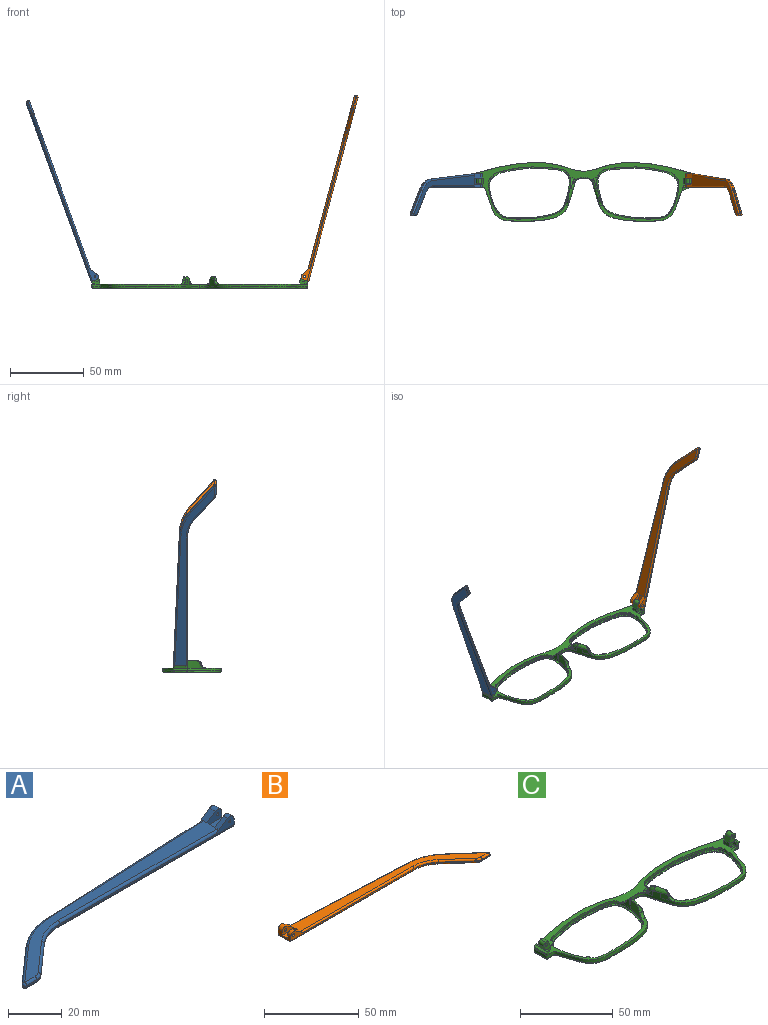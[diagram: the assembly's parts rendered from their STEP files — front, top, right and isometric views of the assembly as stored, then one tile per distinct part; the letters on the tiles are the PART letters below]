
ASSEMBLY  parts=3 mates=2
PART A: 43 faces, bbox 130.2x29.5x5.9 mm
  f0: plane 9.62x3.72mm, normal (1,0,0), area 24.7mm2, adj f1,f3,f4,f5,f10,f16,f18,f28
  f1: cylinder r=2.2mm len=3.45mm, axis (0,-1,0), area 11mm2, adj f0,f2,f4,f37
  f2: plane 6.01x3.91mm, normal (-0.55,0,0.84), area 12.7mm2, adj f1,f4,f9,f19,f37
  f3: plane 2.26x0.1mm, normal (0,0,1), area 0.1mm2, adj f0,f5,f18
  f4: plane 92.1x4.9mm, normal (0,-1,0), area 79.9mm2, adj f0,f1,f2,f14,f19,f36,f42
  f5: plane 93.42x4.13mm, normal (-0.04,1,0), area 64.8mm2, adj f0,f3,f11,f15,f17,f27,f28
  f6: plane 17.82x15.72mm, normal (-0.66,0.75,0), area 14.3mm2, adj f11,f12,f25,f30
  f7: plane 5.46x0.6mm, normal (0,-1,0), area 3.3mm2, adj f12,f13,f23,f32
  f8: plane 14.99x13.23mm, normal (0.66,-0.75,0), area 12mm2, adj f13,f14,f21,f34
  f9: plane 121.18x26.73mm, normal (0,0,1), area 627.7mm2, adj f2,f17,f19,f20,f21,f22,f23,f25
  f10: plane 129.1x27.08mm, normal (0,0,-1), area 686.5mm2, adj f0,f28,f29,f30,f32,f33,f34,f35
  f11: cylinder r=30mm len=18.52mm, axis (0,0,-1), area 12.2mm2, adj f5,f6,f26,f29
  f12: cylinder r=1mm len=1.75mm, axis (0,0,-1), area 1.5mm2, adj f6,f7,f24,f31
  f13: cylinder r=5mm len=3.31mm, axis (0,0,-1), area 2.2mm2, adj f7,f8,f22,f33
  f14: cylinder r=20mm len=13.23mm, axis (0,0,1), area 8.7mm2, adj f4,f8,f20,f35
  f15: plane 5.66x0.25mm, normal (0,0,-1), area 0.7mm2, adj f5,f17,f18
  f16: cylinder r=2.2mm len=3.45mm, axis (0,-1,0), area 14.8mm2, adj f0,f17,f18,f38
  f17: plane 6.01x3.91mm, normal (-0.55,0,0.84), area 16.9mm2, adj f5,f9,f15,f16,f18,f27,f38
  f18: plane 7.92x3.3mm, normal (0,1,0), area 15.9mm2, adj f0,f3,f15,f16,f17,f41
  f19: cylinder r=1mm len=84.18mm, axis (-1,0,0), area 131.4mm2, adj f2,f4,f9,f20
  f20: torus R=21mm, axis (0,0,1), area 23.1mm2, adj f9,f14,f19,f21
  f21: cylinder r=1mm len=15.65mm, axis (-0.75,-0.66,0), area 31.4mm2, adj f8,f9,f20,f22
  f22: torus R=4mm, axis (0,0,1), area 5.3mm2, adj f9,f13,f21,f23
  f23: cylinder r=1mm len=5.46mm, axis (-1,0,0), area 8.6mm2, adj f7,f9,f22,f24
  f24: sphere r=1mm, area 2.4mm2, adj f12,f23,f25
  f25: cylinder r=1mm len=18.48mm, axis (0.75,0.66,0), area 37.3mm2, adj f6,f9,f24,f26
  f26: torus R=29mm, axis (0,0,1), area 31.6mm2, adj f9,f11,f25,f27
  f27: cylinder r=1mm len=85.5mm, axis (1,0.04,0), area 133.5mm2, adj f5,f9,f17,f26
  f28: cylinder r=1mm len=93.46mm, axis (-1,-0.04,0), area 146.9mm2, adj f0,f5,f10,f29
  f29: torus R=29mm, axis (0,0,1), area 31.6mm2, adj f10,f11,f28,f30
  f30: cylinder r=1mm len=18.48mm, axis (-0.75,-0.66,0), area 37.3mm2, adj f6,f10,f29,f31
  f31: sphere r=1mm, area 2.4mm2, adj f12,f30,f32
  f32: cylinder r=1mm len=5.46mm, axis (1,0,0), area 8.6mm2, adj f7,f10,f31,f33
  f33: torus R=4mm, axis (0,0,1), area 5.3mm2, adj f10,f13,f32,f34
  f34: cylinder r=1mm len=15.65mm, axis (0.75,0.66,0), area 31.4mm2, adj f8,f10,f33,f35
  f35: torus R=21mm, axis (0,0,1), area 23.1mm2, adj f10,f14,f34,f36
  f36: cylinder r=1mm len=92.1mm, axis (1,0,0), area 144.7mm2, adj f0,f4,f10,f35
  f37: plane 7.92x4.7mm, normal (0,1,0), area 27mm2, adj f0,f1,f2,f39,f40,f42
  f38: plane 7.92x4.7mm, normal (0,-1,0), area 27mm2, adj f0,f16,f17,f39,f40,f41
  f39: plane 7.92x4.1mm, normal (0,0,1), area 32.5mm2, adj f0,f37,f38,f40
  f40: plane 4.1x1.4mm, normal (1,0,0), area 5.7mm2, adj f9,f37,f38,f39
  f41: cylinder r=0.5mm len=3.1mm, axis (0,-1,0), area 9.7mm2, adj f18,f38
  f42: cylinder r=0.5mm len=2.3mm, axis (0,-1,0), area 7.2mm2, adj f4,f37
PART B: 43 faces, bbox 130.2x29.5x5.9 mm
  f0: plane 9.62x3.72mm, normal (-1,0,0), area 24.7mm2, adj f1,f3,f4,f5,f10,f16,f18,f28
  f1: cylinder r=2.2mm len=3.45mm, axis (0,-1,0), area 11mm2, adj f0,f2,f4,f37
  f2: plane 6.01x3.91mm, normal (0.55,0,0.84), area 12.7mm2, adj f1,f4,f9,f19,f37
  f3: plane 2.26x0.1mm, normal (0,0,1), area 0.1mm2, adj f0,f5,f18
  f4: plane 92.1x4.9mm, normal (0,-1,0), area 78.2mm2, adj f0,f1,f2,f14,f19,f36,f42
  f5: plane 93.42x4.13mm, normal (0.04,1,0), area 64.8mm2, adj f0,f3,f11,f15,f17,f27,f28
  f6: plane 17.82x15.72mm, normal (0.66,0.75,0), area 14.3mm2, adj f11,f12,f25,f30
  f7: plane 5.46x0.6mm, normal (0,-1,0), area 3.3mm2, adj f12,f13,f23,f32
  f8: plane 14.99x13.23mm, normal (-0.66,-0.75,0), area 12mm2, adj f13,f14,f21,f34
  f9: plane 121.18x26.73mm, normal (0,0,1), area 627.7mm2, adj f2,f17,f19,f20,f21,f22,f23,f25
  f10: plane 129.1x27.08mm, normal (0,0,-1), area 686.5mm2, adj f0,f28,f29,f30,f32,f33,f34,f35
  f11: cylinder r=30mm len=18.52mm, axis (0,0,-1), area 12.2mm2, adj f5,f6,f26,f29
  f12: cylinder r=1mm len=1.75mm, axis (0,0,-1), area 1.5mm2, adj f6,f7,f24,f31
  f13: cylinder r=5mm len=3.31mm, axis (0,0,-1), area 2.2mm2, adj f7,f8,f22,f33
  f14: cylinder r=20mm len=13.23mm, axis (0,0,1), area 8.7mm2, adj f4,f8,f20,f35
  f15: plane 5.66x0.25mm, normal (0,0,-1), area 0.7mm2, adj f5,f17,f18
  f16: cylinder r=2.2mm len=3.45mm, axis (0,-1,0), area 14.8mm2, adj f0,f17,f18,f38
  f17: plane 6.01x3.91mm, normal (0.55,0,0.84), area 16.9mm2, adj f5,f9,f15,f16,f18,f27,f38
  f18: plane 7.92x3.3mm, normal (0,1,0), area 14.3mm2, adj f0,f3,f15,f16,f17,f41
  f19: cylinder r=1mm len=84.18mm, axis (1,0,0), area 131.4mm2, adj f2,f4,f9,f20
  f20: torus R=21mm, axis (0,0,1), area 23.1mm2, adj f9,f14,f19,f21
  f21: cylinder r=1mm len=15.65mm, axis (0.75,-0.66,0), area 31.4mm2, adj f8,f9,f20,f22
  f22: torus R=4mm, axis (0,0,1), area 5.3mm2, adj f9,f13,f21,f23
  f23: cylinder r=1mm len=5.46mm, axis (1,0,0), area 8.6mm2, adj f7,f9,f22,f24
  f24: sphere r=1mm, area 2.4mm2, adj f12,f23,f25
  f25: cylinder r=1mm len=18.48mm, axis (-0.75,0.66,0), area 37.3mm2, adj f6,f9,f24,f26
  f26: torus R=29mm, axis (0,0,1), area 31.6mm2, adj f9,f11,f25,f27
  f27: cylinder r=1mm len=85.5mm, axis (-1,0.04,0), area 133.5mm2, adj f5,f9,f17,f26
  f28: cylinder r=1mm len=93.46mm, axis (1,-0.04,0), area 146.9mm2, adj f0,f5,f10,f29
  f29: torus R=29mm, axis (0,0,1), area 31.6mm2, adj f10,f11,f28,f30
  f30: cylinder r=1mm len=18.48mm, axis (0.75,-0.66,0), area 37.3mm2, adj f6,f10,f29,f31
  f31: sphere r=1mm, area 2.4mm2, adj f12,f30,f32
  f32: cylinder r=1mm len=5.46mm, axis (-1,0,0), area 8.6mm2, adj f7,f10,f31,f33
  f33: torus R=4mm, axis (0,0,1), area 5.3mm2, adj f10,f13,f32,f34
  f34: cylinder r=1mm len=15.65mm, axis (-0.75,0.66,0), area 31.4mm2, adj f8,f10,f33,f35
  f35: torus R=21mm, axis (0,0,1), area 23.1mm2, adj f10,f14,f34,f36
  f36: cylinder r=1mm len=92.1mm, axis (-1,0,0), area 144.7mm2, adj f0,f4,f10,f35
  f37: plane 7.92x4.7mm, normal (0,1,0), area 25.4mm2, adj f0,f1,f2,f39,f40,f42
  f38: plane 7.92x4.7mm, normal (0,-1,0), area 25.4mm2, adj f0,f16,f17,f39,f40,f41
  f39: plane 7.92x4.1mm, normal (0,0,1), area 32.5mm2, adj f0,f37,f38,f40
  f40: plane 4.1x1.4mm, normal (-1,0,0), area 5.7mm2, adj f9,f37,f38,f39
  f41: cylinder r=0.88mm len=3.1mm, axis (0,-1,0), area 17mm2, adj f18,f38
  f42: cylinder r=0.88mm len=2.3mm, axis (0,-1,0), area 12.6mm2, adj f4,f37
PART C: 118 faces, bbox 148.1x40.9x17.9 mm
  f0: bspline ~1.82x1.22mm, area 0.7mm2, adj f2,f7,f37,f52
  f1: plane 147.69x40.46mm, normal (0,0,1), area 858.2mm2, adj f4,f5,f6,f7,f8,f12,f20,f23
  f2: bspline ~6.1x4.93mm, area 12.7mm2, adj f0,f7,f37,f41,f43,f52,f53
  f3: plane 4.46x1.45mm, normal (0,0,1), area 0.1mm2, adj f7,f38
  f4: plane 1.23x0.04mm, normal (0,0,1), area 0mm2, adj f1,f7,f22
  f5: plane 6.97x5.07mm, normal (0,1,0), area 22.7mm2, adj f1,f20,f21,f25,f27,f28,f30,f31
  f6: plane 3.2x2.36mm, normal (0,-1,0), area 5.7mm2, adj f1,f20,f26,f29
  f7: extruded ~73.26x39.84mm, area 292.7mm2, adj f0,f1,f2,f3,f4,f8,f13,f14
  f8: extruded ~35.39x5.69mm, area 72.2mm2, adj f1,f7,f18,f67
  f9: plane 144.78x37.85mm, normal (0,0,-1), area 582.4mm2, adj f13,f15,f17,f18,f19,f71,f73,f75
  f10: plane 56.06x35.45mm, normal (0,0,1), area 127mm2, adj f11,f19
  f11: extruded ~55.69x35.36mm, area 160.5mm2, adj f10,f12
  f12: extruded ~55.69x35.36mm, area 226.3mm2, adj f1,f11,f39,f40,f41,f42,f43,f44
  f13: bspline ~73.27x30.39mm, area 161.7mm2, adj f7,f9,f14,f71
  f14: bspline ~1x1mm, area 0.8mm2, adj f7,f13,f15
  f15: bspline ~8.99x1.23mm, area 12.6mm2, adj f7,f9,f14,f16
  f16: bspline ~1.04x1mm, area 0.7mm2, adj f7,f15,f17
  f17: bspline ~45.86x8.59mm, area 59.8mm2, adj f7,f9,f16,f18
  f18: bspline ~37.01x6.7mm, area 56.6mm2, adj f8,f9,f17,f76
  f19: bspline ~56.23x35.9mm, area 235.3mm2, adj f9,f10
  f20: plane 4x2.36mm, normal (-1,0,0), area 9.5mm2, adj f1,f5,f6,f21
  f21: plane 4x0.02mm, normal (0.34,0,0.94), area 0.1mm2, adj f5,f20,f28
  f22: plane 2.76x2.53mm, normal (0,-1,0), area 3.9mm2, adj f4,f26,f27,f35,f56
  f23: plane 7.67x1.6mm, normal (0.94,0,-0.34), area 13mm2, adj f1,f35,f36,f56
  f24: plane 2.1x1.69mm, normal (0,1,0), area 2.8mm2, adj f1,f25,f27,f36,f56
  f25: plane 3.3x2.1mm, normal (-1,0,0), area 6.9mm2, adj f1,f5,f24,f27
  f26: plane 2.35x2.1mm, normal (-1,0,0), area 4.9mm2, adj f1,f6,f22,f27,f29
  f27: plane 9.65x1.24mm, normal (0,0,1), area 8.2mm2, adj f5,f22,f24,f25,f26,f29,f30,f56
  f28: plane 4x3.31mm, normal (-0.94,0,0.34), area 14.1mm2, adj f5,f21,f29,f32
  f29: plane 5.77x5.06mm, normal (0,-1,0), area 17mm2, adj f6,f26,f27,f28,f30,f31,f32,f33
  f30: plane 4x2.21mm, normal (0.94,0,-0.34), area 9.4mm2, adj f5,f27,f29,f33
  f31: plane 4x0.01mm, normal (0.34,0,0.94), area 0mm2, adj f5,f29,f32,f33
  f32: cylinder r=1.98mm len=4mm, axis (0,1,0), area 12.4mm2, adj f5,f28,f29,f31
  f33: cylinder r=1.98mm len=4mm, axis (0,-1,0), area 12.4mm2, adj f5,f29,f30,f31
  f34: cylinder r=0.88mm len=4mm, axis (0,-1,0), area 22mm2, adj f5,f29
  f35: cone r=1mm half-angle=20deg, axis (0,0,1), area 2.3mm2, adj f1,f22,f23,f56
  f36: cylinder r=1mm len=2.28mm, axis (-0.34,0,-0.94), area 3mm2, adj f1,f23,f24,f56
  f37: extruded ~3.67x3.11mm, area 5.9mm2, adj f0,f2,f7,f59
  f38: extruded ~4.44x3.32mm, area 15.1mm2, adj f3,f7,f42,f43,f55
  f39: extruded ~4.98x1.37mm, area 6.6mm2, adj f12,f41
  f40: plane 3.63x0.97mm, normal (0,0,1), area 0.3mm2, adj f12,f41,f43
  f41: bspline ~15.5x15.35mm, area 6.4mm2, adj f2,f12,f39,f40,f54
  f42: bspline ~7.26x7.26mm, area 6.3mm2, adj f12,f38,f43,f55
  f43: bspline ~10.29x4.84mm, area 21.4mm2, adj f2,f7,f12,f38,f40,f42
  f44: plane 3.19x1.37mm, normal (0,0,-1), area 2.1mm2, adj f12,f45
  f45: cylinder r=2.28mm len=3.17mm, axis (0,0,1), area 2.1mm2, adj f1,f12,f44,f54
  f46: plane 3.14x2.79mm, normal (0,0,-1), area 3.9mm2, adj f12,f47
  f47: cylinder r=2.28mm len=3.13mm, axis (0,0,1), area 2.5mm2, adj f1,f12,f46
  f48: plane 1.79x1.31mm, normal (0,0,-1), area 0.9mm2, adj f12,f49
  f49: cylinder r=1.3mm len=1.78mm, axis (0,0,1), area 1.3mm2, adj f1,f12,f48
  f50: plane 1.95x1.68mm, normal (0,0,-1), area 1.5mm2, adj f12,f51
  f51: cylinder r=1.3mm len=1.93mm, axis (0,0,1), area 1.5mm2, adj f1,f12,f50
  f52: bspline ~2.66x2.04mm, area 1.9mm2, adj f0,f2,f7,f53,f58
  f53: bspline ~3.55x3.47mm, area 3.7mm2, adj f1,f2,f52,f54,f58
  f54: bspline ~6.16x4.45mm, area 7.9mm2, adj f1,f12,f41,f45,f53
  f55: bspline ~3.7x3.66mm, area 7.8mm2, adj f1,f7,f12,f38,f42
  f56: plane 9.71x1.44mm, normal (0.34,0,0.94), area 13.9mm2, adj f22,f23,f24,f27,f35,f36
  f57: bspline ~6.38x2.14mm, area 2.6mm2, adj f1,f7,f58,f115
  f58: bspline ~2.1x1.46mm, area 0.6mm2, adj f7,f52,f53,f57
  f59: bspline ~5.24x1.75mm, area 0mm2, adj f7,f37
  f60: bspline ~2.19x1.4mm, area 0.7mm2, adj f61,f66,f95,f110
  f61: bspline ~6.1x4.93mm, area 12.6mm2, adj f60,f66,f95,f99,f101,f110,f111
  f62: plane 4.46x1.45mm, normal (0,0,1), area 0.1mm2, adj f66,f96
  f63: plane 1.23x0.04mm, normal (0,0,1), area 0mm2, adj f1,f66,f80
  f64: plane 6.97x5.07mm, normal (0,1,0), area 22.7mm2, adj f1,f78,f79,f83,f85,f86,f88,f89
  f65: plane 3.2x2.36mm, normal (0,-1,0), area 5.7mm2, adj f1,f78,f84,f87
  f66: extruded ~73.26x39.84mm, area 292.7mm2, adj f1,f7,f60,f61,f62,f63,f67,f71
  f67: extruded ~35.39x5.69mm, area 72.2mm2, adj f1,f8,f66,f76
  f68: plane 56.06x35.45mm, normal (0,0,1), area 127mm2, adj f69,f77
  f69: extruded ~55.69x35.36mm, area 160.5mm2, adj f68,f70
  f70: extruded ~55.69x35.36mm, area 226.4mm2, adj f1,f69,f97,f98,f99,f100,f101,f102
  f71: bspline ~73.83x30.39mm, area 161.7mm2, adj f9,f13,f66,f72
  f72: bspline ~1x1mm, area 0.8mm2, adj f66,f71,f73
  f73: bspline ~8.99x1.23mm, area 12.6mm2, adj f9,f66,f72,f74
  f74: bspline ~1.04x1mm, area 0.8mm2, adj f66,f73,f75
  f75: bspline ~45.86x8.59mm, area 59.8mm2, adj f9,f66,f74,f76
  f76: bspline ~37.01x6.7mm, area 56.6mm2, adj f9,f18,f67,f75
  f77: bspline ~56.22x35.9mm, area 235.3mm2, adj f9,f68
  f78: plane 4x2.36mm, normal (1,0,0), area 9.5mm2, adj f1,f64,f65,f79
  f79: plane 4x0.02mm, normal (-0.34,0,0.94), area 0.1mm2, adj f64,f78,f86
  f80: plane 2.76x2.53mm, normal (0,-1,0), area 3.9mm2, adj f63,f84,f85,f93,f114
  f81: plane 7.67x1.6mm, normal (-0.94,0,-0.34), area 13mm2, adj f1,f93,f94,f114
  f82: plane 2.1x1.69mm, normal (0,1,0), area 2.8mm2, adj f1,f83,f85,f94,f114
  f83: plane 3.3x2.1mm, normal (1,0,0), area 6.9mm2, adj f1,f64,f82,f85
  f84: plane 2.35x2.1mm, normal (1,0,0), area 4.9mm2, adj f1,f65,f80,f85,f87
  f85: plane 9.65x1.24mm, normal (0,0,1), area 8.2mm2, adj f64,f80,f82,f83,f84,f87,f88,f114
  f86: plane 4x3.31mm, normal (0.94,0,0.34), area 14.1mm2, adj f64,f79,f87,f90
  f87: plane 5.77x5.06mm, normal (0,-1,0), area 17mm2, adj f65,f84,f85,f86,f88,f89,f90,f91
  f88: plane 4x2.21mm, normal (-0.94,0,-0.34), area 9.4mm2, adj f64,f85,f87,f91
  f89: plane 4x0.01mm, normal (-0.34,0,0.94), area 0mm2, adj f64,f87,f90,f91
  f90: cylinder r=1.98mm len=4mm, axis (0,1,0), area 12.4mm2, adj f64,f86,f87,f89
  f91: cylinder r=1.98mm len=4mm, axis (0,-1,0), area 12.4mm2, adj f64,f87,f88,f89
  f92: cylinder r=0.88mm len=4mm, axis (0,-1,0), area 22mm2, adj f64,f87
  f93: cone r=1mm half-angle=20deg, axis (0,0,1), area 2.3mm2, adj f1,f80,f81,f114
  f94: cylinder r=1mm len=2.28mm, axis (0.34,0,-0.94), area 3mm2, adj f1,f81,f82,f114
  f95: extruded ~3.67x3.11mm, area 5.9mm2, adj f60,f61,f66,f117
  f96: extruded ~4.44x3.32mm, area 15.1mm2, adj f62,f66,f100,f101,f113
  f97: extruded ~4.98x1.36mm, area 6.6mm2, adj f70,f99
  f98: plane 3.63x0.97mm, normal (0,0,1), area 0.3mm2, adj f70,f99,f101
  f99: bspline ~15.5x15.35mm, area 6.4mm2, adj f61,f70,f97,f98,f112
  f100: bspline ~7.26x7.26mm, area 6.2mm2, adj f70,f96,f101,f113
  f101: bspline ~10.29x4.84mm, area 21.5mm2, adj f61,f66,f70,f96,f98,f100
  f102: plane 3.19x1.37mm, normal (0,0,-1), area 2.1mm2, adj f70,f103
  f103: cylinder r=2.28mm len=3.17mm, axis (0,0,1), area 2.1mm2, adj f1,f70,f102,f112
  f104: plane 3.14x2.79mm, normal (0,0,-1), area 3.9mm2, adj f70,f105
  f105: cylinder r=2.28mm len=3.13mm, axis (0,0,1), area 2.5mm2, adj f1,f70,f104
  f106: plane 1.79x1.31mm, normal (0,0,-1), area 0.9mm2, adj f70,f107
  f107: cylinder r=1.3mm len=1.78mm, axis (0,0,1), area 1.3mm2, adj f1,f70,f106
  f108: plane 1.95x1.68mm, normal (0,0,-1), area 1.5mm2, adj f70,f109
  f109: cylinder r=1.3mm len=1.93mm, axis (0,0,1), area 1.5mm2, adj f1,f70,f108
  f110: bspline ~2.65x2.03mm, area 1.9mm2, adj f60,f61,f66,f111,f116
  f111: bspline ~3.55x3.47mm, area 3.7mm2, adj f1,f61,f110,f112,f116
  f112: bspline ~5.94x4.42mm, area 7.9mm2, adj f1,f70,f99,f103,f111
  f113: bspline ~3.7x3.66mm, area 7.8mm2, adj f1,f66,f70,f96,f100
  f114: plane 9.71x1.44mm, normal (-0.34,0,0.94), area 13.9mm2, adj f80,f81,f82,f85,f93,f94
  f115: bspline ~6.38x2.14mm, area 2.6mm2, adj f1,f57,f66,f116
  f116: bspline ~2.1x1.46mm, area 0.6mm2, adj f66,f110,f111,f115
  f117: bspline ~5.24x1.75mm, area 0mm2, adj f66,f95
PLACE A rot(axis=(0,1,0),70deg) t=(-56.09,8.44,52.45)mm
PLACE B rot(axis=(0,-1,0),75deg) t=(96.87,8.44,-65.16)mm
PLACE C t=(38.82,13.05,-9.32)mm
MATE revolute A.f1 <-> C.f90  axis (0,-1,0) through (-32.22,16.9,-2.33)mm
MATE revolute B.f41 <-> C.f33  axis (0,-1,0) through (109.88,16.9,-2.34)mm
